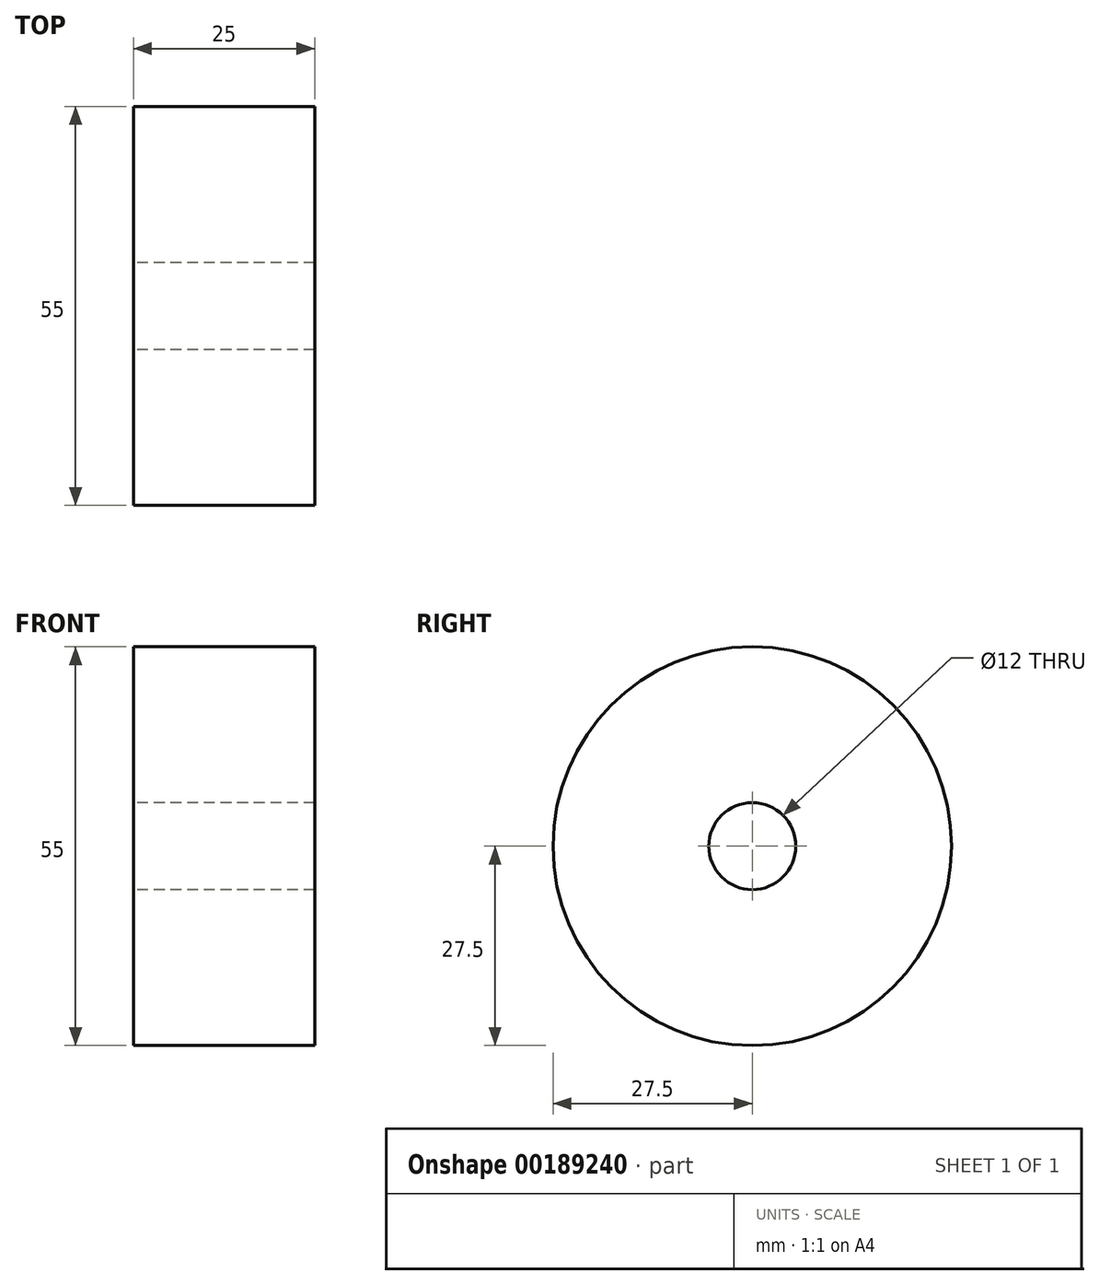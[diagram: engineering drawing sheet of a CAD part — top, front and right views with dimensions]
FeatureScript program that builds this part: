
annotation { "Feature Type Name" : "Feature", "Feature Type Description" : "" }
export const myFeature = defineFeature(function(context is Context, id is Id, definition is map)
    precondition{}
    {
        {
            var Q0;
            Q0=qCreatedBy(makeId("Right.planeOp"),FACE);
            var sketch = newSketch(context, id + "F0", { "sketchPlane" : qUnion([Q0])});
            skCircle(sketch, "E0", {"center": v(0, 0) * mm, "radius": 27.5 * mm});
            skCircle(sketch, "E1", {"center": v(0, 0) * mm, "radius": 6 * mm});
            skSolve(sketch);
        }
        {
            var Q0;
            Q0=makeQuery(id+"F0.imprint","IMPRINT",FACE,{"disambiguationData":[TD([[makeQuery(id+"F0.imprint","IMPRINT",EDGE,{"derivedFrom":sQuery(id+"F0.wireOp",EDGE,"E0")}),1.0]])]});
            extrude(context, id + "F1", {"entities" : qUnion([Q0]), "depth" : 25 * mm});
        }
    });
